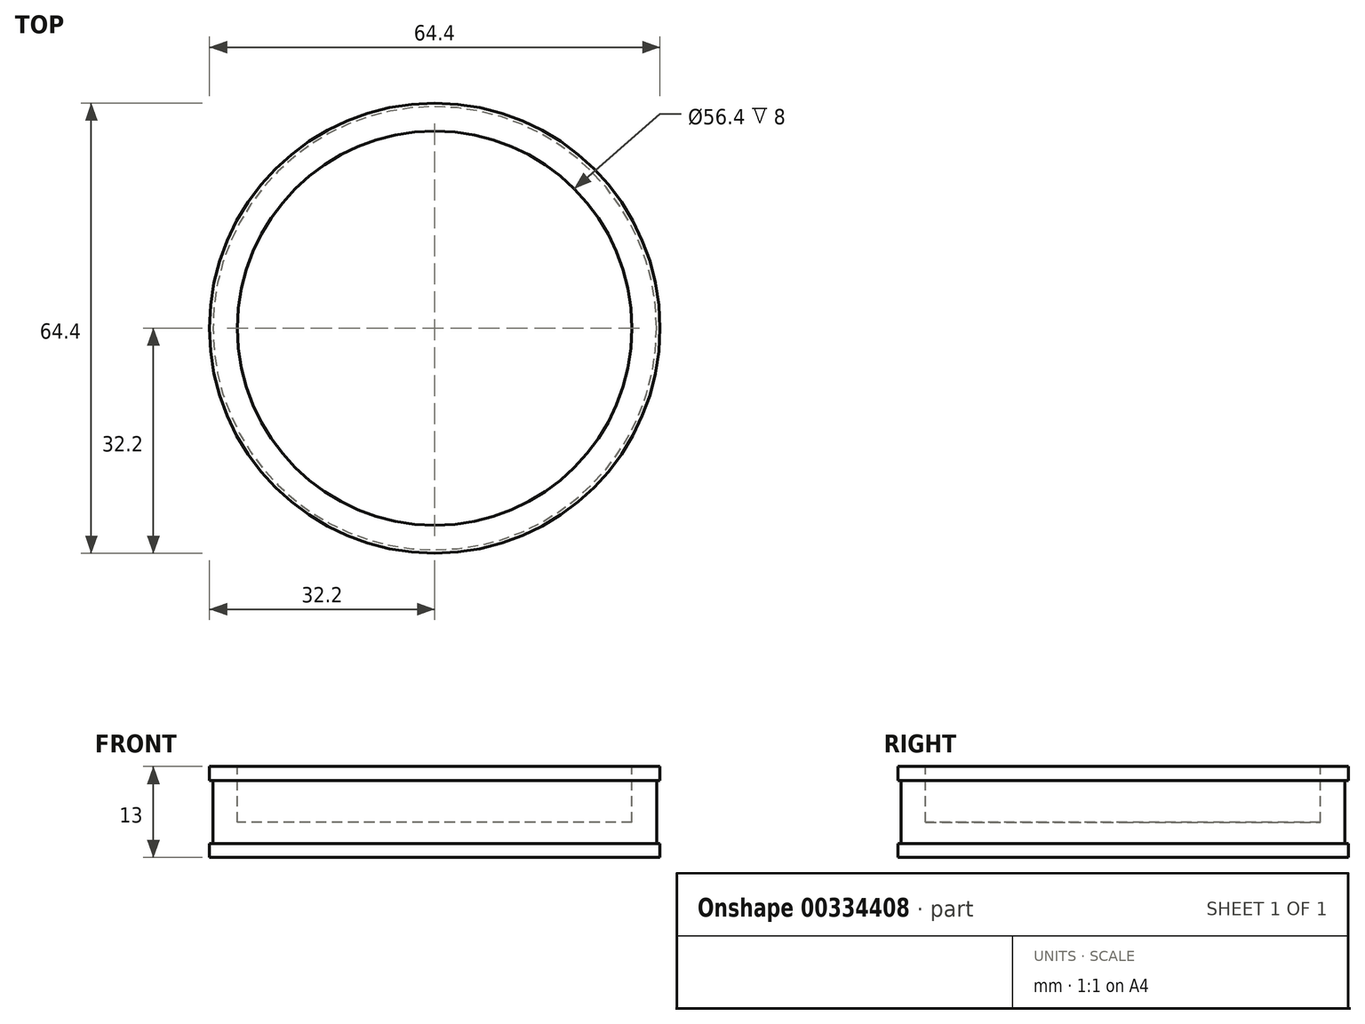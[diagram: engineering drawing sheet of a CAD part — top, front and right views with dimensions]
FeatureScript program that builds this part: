
annotation { "Feature Type Name" : "Feature", "Feature Type Description" : "" }
export const myFeature = defineFeature(function(context is Context, id is Id, definition is map)
    precondition{}
    {
        {
            var Q0;
            Q0=qCreatedBy(makeId("Front.planeOp"),FACE);
            var sketch = newSketch(context, id + "F0", { "sketchPlane" : qUnion([Q0])});
            skLineSegment(sketch, "E0", {"start": v(0, 0) * mm, "end": v(32.2, 0) * mm});
            skLineSegment(sketch, "E1", {"start": v(32.2, 0) * mm, "end": v(32.2, 2) * mm});
            skLineSegment(sketch, "E2", {"start": v(32.2, 2) * mm, "end": v(31.7, 2) * mm});
            skLineSegment(sketch, "E3", {"start": v(31.7, 2) * mm, "end": v(31.7, 11) * mm});
            skLineSegment(sketch, "E4", {"start": v(31.7, 11) * mm, "end": v(32.2, 11) * mm});
            skLineSegment(sketch, "E5", {"start": v(32.2, 11) * mm, "end": v(32.2, 13) * mm});
            skLineSegment(sketch, "E6", {"start": v(32.2, 13) * mm, "end": v(28.2, 13) * mm});
            skLineSegment(sketch, "E7", {"start": v(28.2, 13) * mm, "end": v(28.2, 5) * mm});
            skLineSegment(sketch, "E8", {"start": v(28.2, 5) * mm, "end": v(0, 5) * mm});
            skLineSegment(sketch, "E9", {"start": v(0, 5) * mm, "end": v(0, 0) * mm});
            skSolve(sketch);
        }
        {
            var Q0;
            Q0=makeQuery(id+"F0.imprint","IMPRINT",FACE,{"disambiguationData":[TD([[makeQuery(id+"F0.imprint","IMPRINT",EDGE,{"derivedFrom":sQuery(id+"F0.wireOp",EDGE,"E0")}),1.0]])]});
            var Q1;
            Q1=sQuery(id+"F0.wireOp",EDGE,"E9");
            revolve(context, id + "F1", {"entities" : qUnion([Q0]), "axis" : qUnion([Q1]), "revolveType" : RevolveType.FULL});
        }
    });
